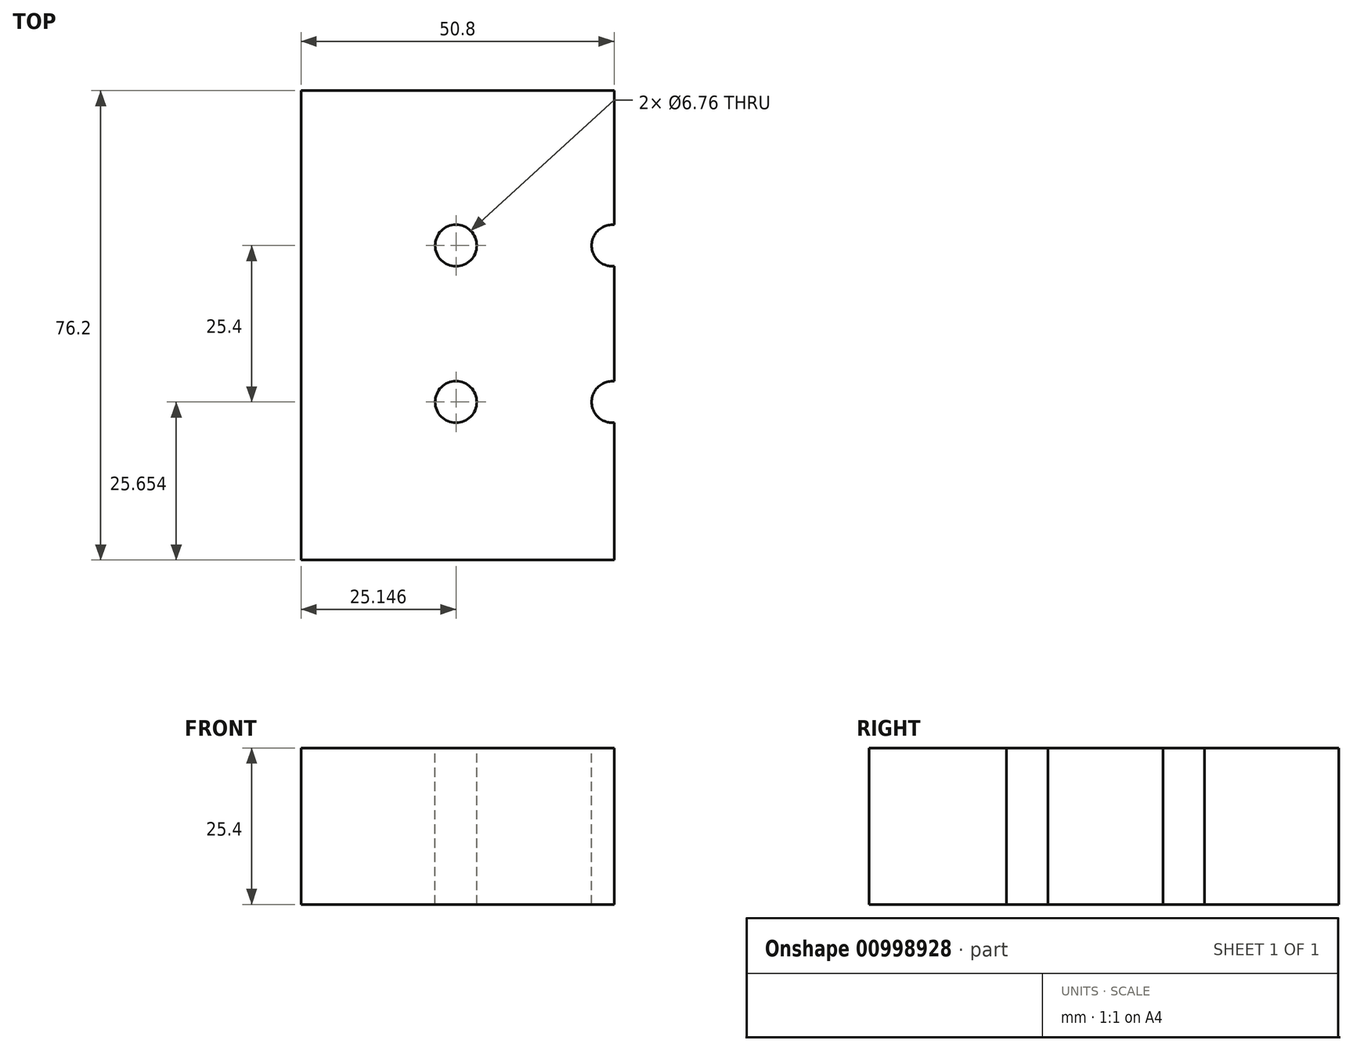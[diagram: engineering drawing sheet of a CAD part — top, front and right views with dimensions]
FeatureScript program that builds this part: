
annotation { "Feature Type Name" : "Feature", "Feature Type Description" : "" }
export const myFeature = defineFeature(function(context is Context, id is Id, definition is map)
    precondition{}
    {
        {
            var Q0;
            Q0=qCreatedBy(makeId("Front.planeOp"),FACE);
            var sketch = newSketch(context, id + "F0", { "sketchPlane" : qUnion([Q0])});
            skLineSegment(sketch, "E0.bottom", {"start": v(0, 0) * mm, "end": v(50.8, 0) * mm});
            skLineSegment(sketch, "E0.top", {"start": v(0, 25.4) * mm, "end": v(50.8, 25.4) * mm});
            skLineSegment(sketch, "E0.left", {"start": v(0, 0) * mm, "end": v(0, 25.4) * mm});
            skLineSegment(sketch, "E0.right", {"start": v(50.8, 0) * mm, "end": v(50.8, 25.4) * mm});
            skSolve(sketch);
        }
        {
            var Q0;
            Q0=makeQuery(id+"F0.imprint","IMPRINT",FACE,{"disambiguationData":[TD([[makeQuery(id+"F0.imprint","IMPRINT",EDGE,{"derivedFrom":sQuery(id+"F0.wireOp",EDGE,"E0.bottom")}),1.0]])]});
            extrude(context, id + "F1", {"entities" : qUnion([Q0]), "depth" : 76.2 * mm, "offsetDistance" : 25.4 * mm});
        }
        {
            var Q0;
            Q0=makeQuery(id+"F1.opExtrude","SWEPT_FACE",FACE,{"disambiguationData":[OSD([sQuery(id+"F0.wireOp",EDGE,"E0.top")])]});
            var sketch = newSketch(context, id + "F2", { "sketchPlane" : qUnion([Q0])});
            skPoint(sketch, "E1", {"position": v(25.15, -25.15) * mm});
            skPoint(sketch, "E2", {"position": v(50.55, -25.15) * mm});
            skPoint(sketch, "E3", {"position": v(25.15, -50.55) * mm});
            skPoint(sketch, "E4", {"position": v(50.55, -50.55) * mm});
            skSolve(sketch);
        }
        {
            var Q0;
            Q0=sQuery(id+"F2.wireOp",VERTEX,"E1");
            var Q1;
            Q1=sQuery(id+"F2.wireOp",VERTEX,"E2");
            var Q2;
            Q2=sQuery(id+"F2.wireOp",VERTEX,"E4");
            var Q3;
            Q3=sQuery(id+"F2.wireOp",VERTEX,"E3");
            var Q4;
            Q4=makeQuery(id+"F1.opExtrude","SWEPT_BODY",BODY,{"disambiguationData":[OSD([sQuery(id+"F0.wireOp",EDGE,"E0.bottom"),sQuery(id+"F0.wireOp",EDGE,"E0.top"),sQuery(id+"F0.wireOp",EDGE,"E0.left"),sQuery(id+"F0.wireOp",EDGE,"E0.right")])]});
            hole(context, id + "F3", {"style" : HoleStyle.SIMPLE, "endStyle" : HoleEndStyle.BLIND, "standardTappedOrClearance" : lookupTablePath({ "fit" : "Close (ASME)", "standard" : "ANSI", "size" : "1/4", "type" : "Clearance" }), "standardBlindInLast" : lookupTablePath({ "fit" : "Close", "standard" : "ANSI", "engagement" : "75%", "pitch" : "20 tpi", "size" : "1/4", "type" : "Clearance & tapped" }), "holeDiameter" : 6.76 * mm, "majorDiameter" : 6.35 * mm, "holeDepth" : 50.8 * mm, "isTappedThrough" : true, "tappedDepth" : 12.7 * mm, "tapClearance" : 3, "startFromSketch" : true, "locations" : qUnion([Q0, Q1, Q2, Q3]), "scope" : qUnion([Q4])});
        }
    });
